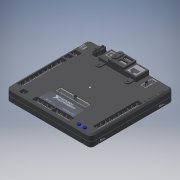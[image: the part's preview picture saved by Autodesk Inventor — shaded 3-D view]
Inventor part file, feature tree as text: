
AUTODESK INVENTOR PART (.ipt)
format: ipt  version: 2016 (Build 200138000, 138)  size: 38,988,800 bytes
history: native  units: in
note: dims shown in document units (in); Inventor stores cm internally (conversion verified against a paired STEP export)
features: imported_body x16, other x3, sketch x2, plane x1
ambient origin geometry x8: Origin, YZ Plane, XZ Plane, XY Plane, X Axis, Y Axis, Z Axis, Center Point
bodies: Solid1 (feature_tree), Solid2 (feature_tree), Solid3 (feature_tree), Solid4 (feature_tree), Solid5 (feature_tree), Solid6 (feature_tree), Solid7 (feature_tree), Solid8 (feature_tree), Solid9 (feature_tree), Solid10 (feature_tree), Solid11 (feature_tree), Solid12 (feature_tree), Solid13 (feature_tree), Solid14 (feature_tree), Solid15 (feature_tree), Solid16 (feature_tree)
feature tree (22):
  other  "cd_roborio1"
  sketch  "Sketch1"
  other  "Decal2"
  plane  "Work Plane1"
  imported_body  "Base1"
  imported_body  "Base2"
  imported_body  "Base3"
  imported_body  "Base4"
  imported_body  "Base5"
  imported_body  "Base6"
  imported_body  "Base7"
  imported_body  "Base8"
  imported_body  "Base9"
  imported_body  "Base10"
  imported_body  "Base11"
  imported_body  "Base12"
  imported_body  "Base13"
  imported_body  "Base14"
  imported_body  "Base15"
  imported_body  "Base16"
  sketch  "Sketch3"
  other  "Image2"
